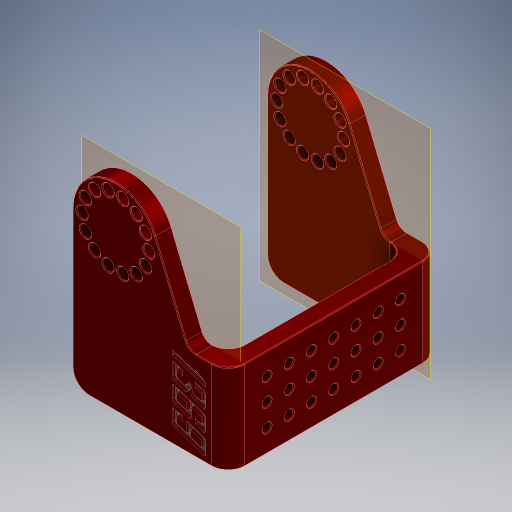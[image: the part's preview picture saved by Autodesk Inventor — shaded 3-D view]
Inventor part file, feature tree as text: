
AUTODESK INVENTOR PART (.ipt)
format: ipt  version: 2024.2 (Build 282272000, 272)  size: 1,318,400 bytes
history: native  units: in
note: dims shown in document units (in); Inventor stores cm internally (conversion verified against a paired STEP export)
features: sketch x7, extrude x7, fillet x3, projected_geometry x3, chamfer x2, plane x1, thicken_offset x1, pattern_linear x1
ambient origin geometry x8: Origin, YZ Plane, XZ Plane, XY Plane, X Axis, Y Axis, Z Axis, Center Point
bodies: Body1 (feature_tree)
feature tree (25):
  sketch  "Sketch6"  dims[d44=1.5in d45=0.25in]
  plane  "Work Plane5"
  extrude  "Extrusion6"  Depth=0.25in
  extrude  "Extrusion7"  Depth=1.925in
  extrude  "Extrusion8"  Depth=1.0in
  extrude  "Extrusion9"  Depth=4.0in
  thicken_offset  "Thicken1"
  fillet  "Fillet1"  Radius=0.125in
  chamfer  "Chamfer1"  Distance=0.125in
  extrude  "Extrusion10"  Depth=1.0in TaperAngle=0.0deg
  chamfer  "Chamfer2"  Distance=0.375in
  pattern_linear  "Rectangular Pattern1"  Spacing1=0.0156in  [1 undecoded]
  sketch  "Sketch12"  dims[d63=0.25in]
  extrude  "Extrusion11"  Depth=0.0197in
  extrude  "Extrusion12"  Depth=0.0197in
  fillet  "Fillet3"  Radius=0.5in
  fillet  "Fillet4"  Radius=1.1811in
  sketch  "Sketch7"  dims[d46=5.5118in d48=360.0deg d50=1.925in]
  sketch  "Sketch8"  dims[d51=3.25in d52=1.0in]
  projected_geometry  "Projected Loop3"
  projected_geometry  "Projected Loop4"
  sketch  "Sketch9"  dims[d53=0.25in d54=4.0in d55=0.125in d56=0.0in d57=0.125in d58=0.0in]
  projected_geometry  "Projected Loop5"
  sketch  "Sketch10"  dims[d59=0.125in d60=0.0in d61=1.0in d62=0.0in]
  sketch  "Sketch13"  dims[d64=0.25in d65=0.375in d67=0.0156in d68=0.125in d69=45.0deg d70=0.196in d71=0.5in d72=0.5in d73=1.1811in d75=0.5in d76=2.7559in d78=0.5in d81=0.8125in d82=0.0in d83=0.0156in d84=0.125in d85=45.0deg d86=1.1811in d88=0.5in d89=2.7559in d91=0.5in d92=0.0591in d93=0.0in d94=0.0591in d95=0.0in d96=0.0197in d97=0.0197in d42=0.5in d43=0.0344in]
note: 1 required parameter value undecoded (feature->parameter linkage not recoverable at this tier; creation-order binding heuristic only, values carry confidence <= 0.55)
